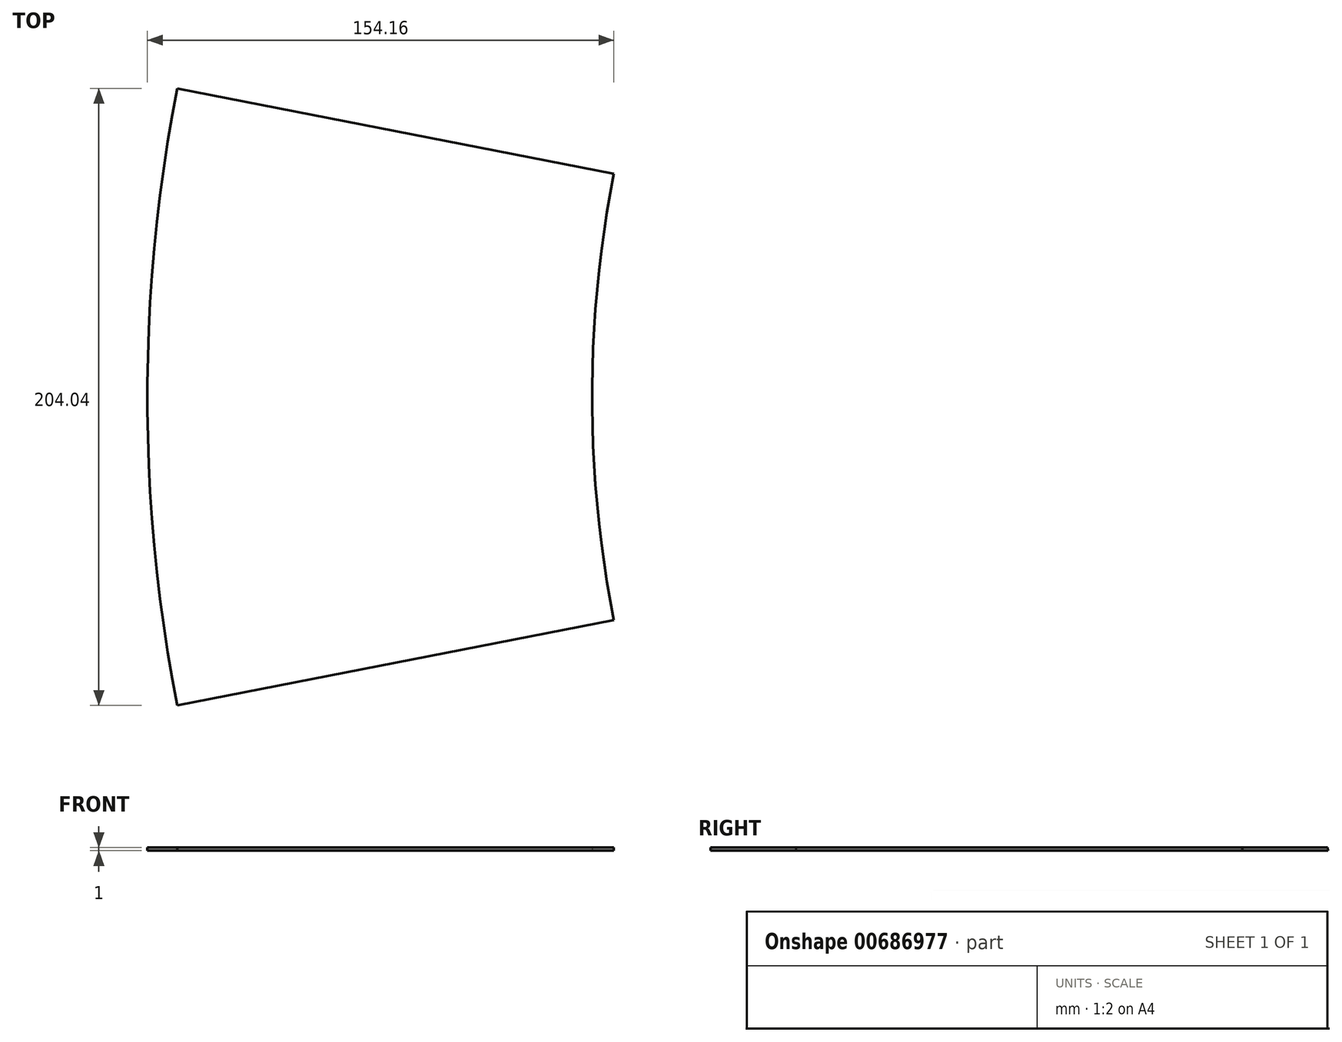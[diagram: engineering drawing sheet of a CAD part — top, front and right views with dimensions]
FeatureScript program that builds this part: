
annotation { "Feature Type Name" : "Feature", "Feature Type Description" : "" }
export const myFeature = defineFeature(function(context is Context, id is Id, definition is map)
    precondition{}
    {
        {
            var Q0;
            Q0=qCreatedBy(makeId("Front.planeOp"),FACE);
            var sketch = newSketch(context, id + "F0", { "sketchPlane" : qUnion([Q0])});
            skLineSegment(sketch, "E0", {"start": v(-0.07, -1.79) * mm, "end": v(534.04, 0) * mm});
            skLineSegment(sketch, "E1", {"start": v(534.04, 0) * mm, "end": v(517.63, 91.28) * mm});
            skLineSegment(sketch, "E2", {"start": v(517.63, 91.28) * mm, "end": v(-0.07, -1.79) * mm});
            skLineSegment(sketch, "E3", {"start": v(517.63, 91.28) * mm, "end": v(493.7, 224.42) * mm});
            skLineSegment(sketch, "E4", {"start": v(493.7, 224.42) * mm, "end": v(-24, 131.35) * mm});
            skArc(sketch, "E5", {"start": v(-24, 131.35) * mm, "mid": v(-12.39, 81.05) * mm, "end": v(4.1, 32.14) * mm});
            skLineSegment(sketch, "E6", {"start": v(4.1, 32.14) * mm, "end": v(493.7, 224.42) * mm});
            skLineSegment(sketch, "E7", {"start": v(4.1, 32.14) * mm, "end": v(9.88, 0) * mm});
            skLineSegment(sketch, "E8", {"start": v(-0.07, -1.79) * mm, "end": v(0, -21.79) * mm});
            skLineSegment(sketch, "E9", {"start": v(0, -21.79) * mm, "end": v(156, -21.27) * mm});
            skLineSegment(sketch, "E10", {"start": v(156, -21.27) * mm, "end": v(155.93, -1.27) * mm});
            skLineSegment(sketch, "E11", {"start": v(4.43, -1.77) * mm, "end": v(4.5, -21.77) * mm});
            skLineSegment(sketch, "E12", {"start": v(151.5, -21.28) * mm, "end": v(151.43, -1.28) * mm});
            skSolve(sketch);
        }
        {
            var Q0;
            {var subQ0=sQuery(id+"F0.wireOp",EDGE,"E11");Q0=makeQuery(id+"F0.imprint","IMPRINT",FACE,{"disambiguationData":[TD([[makeQuery(id+"F0.imprint","IMPRINT",EDGE,{"derivedFrom":subQ0}),1.0]])]});}
            var Q1;
            Q1=sQuery(id+"F0.wireOp",EDGE,"E1");
            revolve(context, id + "F1", {"entities" : qUnion([Q0]), "axis" : qUnion([Q1]), "revolveType" : RevolveType.SYMMETRIC, "angle" : 22.5 * degree});
        }
        {
            var Q0;
            Q0=qCreatedBy(makeId("Front.planeOp"),FACE);
            var sketch = newSketch(context, id + "F2", { "sketchPlane" : qUnion([Q0])});
            skLineSegment(sketch, "E13.bottom", {"start": v(-57.42, 44.28) * mm, "end": v(231.4, 44.28) * mm});
            skLineSegment(sketch, "E13.top", {"start": v(-57.42, -6.8) * mm, "end": v(231.4, -6.8) * mm});
            skLineSegment(sketch, "E13.left", {"start": v(-57.42, 44.28) * mm, "end": v(-57.42, -6.8) * mm});
            skLineSegment(sketch, "E13.right", {"start": v(231.4, 44.28) * mm, "end": v(231.4, -6.8) * mm});
            skLineSegment(sketch, "E14.bottom", {"start": v(-57.42, -7.8) * mm, "end": v(231.4, -7.8) * mm});
            skLineSegment(sketch, "E14.top", {"start": v(-57.42, -85.9) * mm, "end": v(231.4, -85.9) * mm});
            skLineSegment(sketch, "E14.left", {"start": v(-57.42, -7.8) * mm, "end": v(-57.42, -85.9) * mm});
            skLineSegment(sketch, "E14.right", {"start": v(231.4, -7.8) * mm, "end": v(231.4, -85.9) * mm});
            skSolve(sketch);
        }
        {
            var Q0;
            Q0=makeQuery(id+"F2.imprint","IMPRINT",FACE,{"disambiguationData":[TD([[makeQuery(id+"F2.imprint","IMPRINT",EDGE,{"derivedFrom":sQuery(id+"F2.wireOp",EDGE,"E13.bottom")}),-1.0]])]});
            var Q1;
            Q1=makeQuery(id+"F2.imprint","IMPRINT",FACE,{"disambiguationData":[TD([[makeQuery(id+"F2.imprint","IMPRINT",EDGE,{"derivedFrom":sQuery(id+"F2.wireOp",EDGE,"E14.bottom")}),-1.0]])]});
            extrude(context, id + "F3", {"entities" : qUnion([Q0, Q1]), "operationType" : NewBodyOperationType.REMOVE, "endBound" : BoundingType.SYMMETRIC, "oppositeDirection" : true, "depth" : 238 * mm, "offsetDistance" : 25 * mm});
        }
    });
